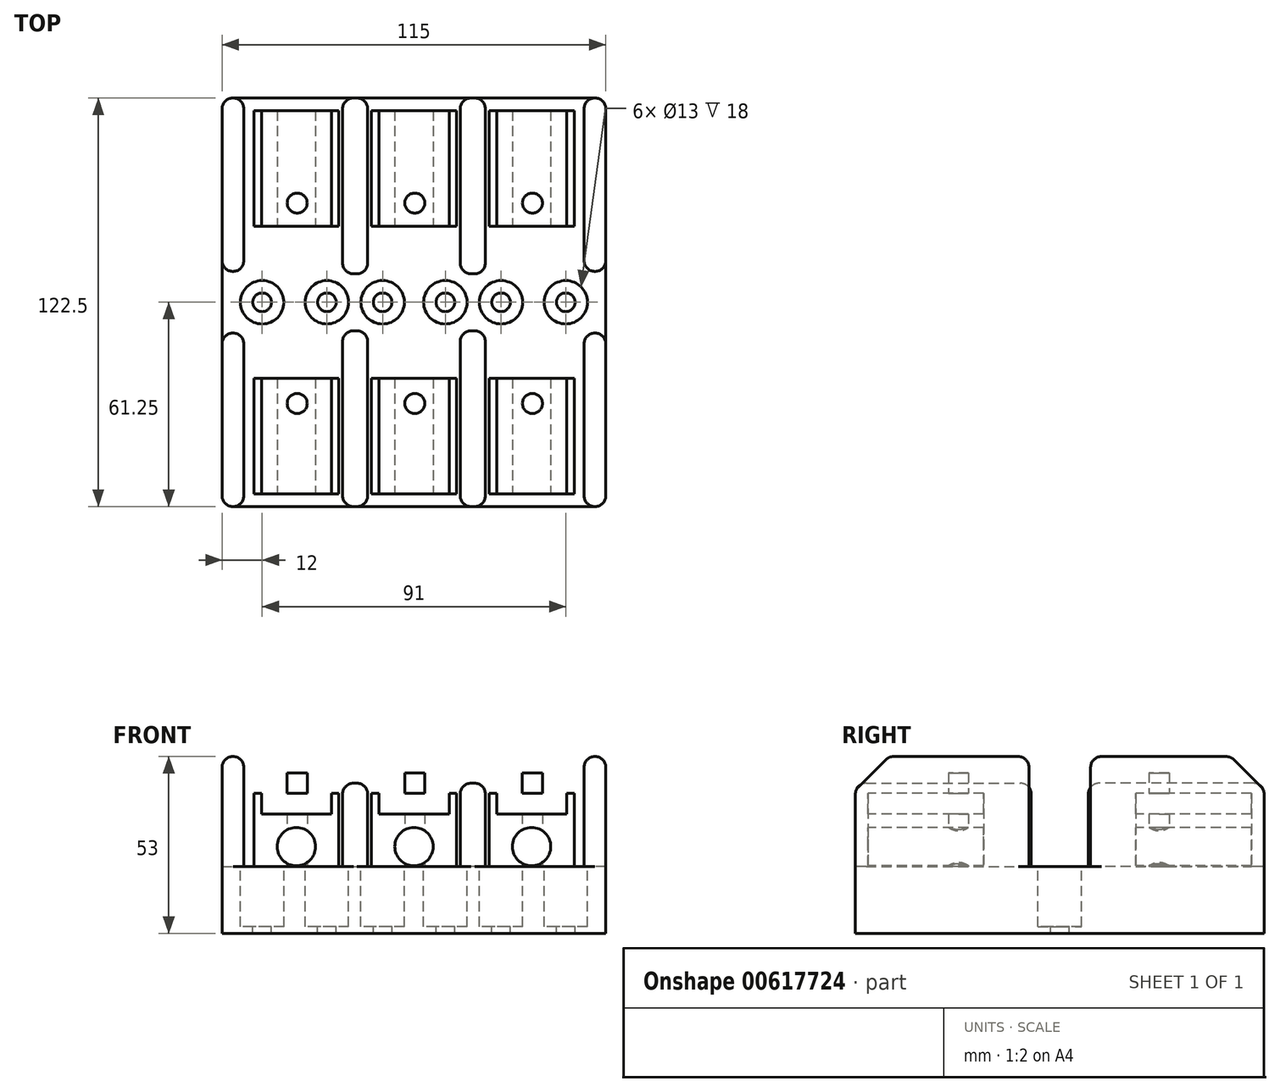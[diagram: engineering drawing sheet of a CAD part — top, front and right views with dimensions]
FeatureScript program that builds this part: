
annotation { "Feature Type Name" : "Feature", "Feature Type Description" : "" }
export const myFeature = defineFeature(function(context is Context, id is Id, definition is map)
    precondition{}
    {
        {
            var Q0;
            Q0=qCreatedBy(makeId("Top.planeOp"),FACE);
            var sketch = newSketch(context, id + "F0", { "sketchPlane" : qUnion([Q0])});
            skLineSegment(sketch, "E0.bottom", {"start": v(0, 0) * mm, "end": v(115, 0) * mm});
            skLineSegment(sketch, "E0.top", {"start": v(0, 122.5) * mm, "end": v(115, 122.5) * mm});
            skLineSegment(sketch, "E0.left", {"start": v(0, 0) * mm, "end": v(0, 122.5) * mm});
            skLineSegment(sketch, "E0.right", {"start": v(115, 0) * mm, "end": v(115, 122.5) * mm});
            skSolve(sketch);
        }
        {
            var Q0;
            Q0 = qSketchRegion(id + "F0", true);
            extrude(context, id + "F1", {"entities" : qUnion([Q0]), "depth" : 20 * mm, "offsetDistance" : 25 * mm});
        }
        {
            var Q0;
            Q0=makeQuery(id+"F1.opExtrude","CAP_FACE",FACE,{"disambiguationData":[OSD([sQuery(id+"F0.wireOp",EDGE,"E0.bottom"),sQuery(id+"F0.wireOp",EDGE,"E0.top"),sQuery(id+"F0.wireOp",EDGE,"E0.left"),sQuery(id+"F0.wireOp",EDGE,"E0.right")])],"isStart":false});
            var sketch = newSketch(context, id + "F2", { "sketchPlane" : qUnion([Q0])});
            skCircle(sketch, "E1", {"center": v(12, 61.25) * mm, "radius": 6.5 * mm});
            skPoint(sketch, "E1.centerSnap0", {"position": v(0, 61.25) * mm});
            skCircle(sketch, "E2", {"center": v(31.4, 61.25) * mm, "radius": 6.5 * mm});
            skCircle(sketch, "E3", {"center": v(48.1, 61.25) * mm, "radius": 6.5 * mm});
            skCircle(sketch, "E4.MirrorC", {"center": v(103, 61.25) * mm, "radius": 6.5 * mm});
            skCircle(sketch, "E5.MirrorC", {"center": v(83.6, 61.25) * mm, "radius": 6.5 * mm});
            skCircle(sketch, "E6.MirrorC", {"center": v(66.9, 61.25) * mm, "radius": 6.5 * mm});
            skSolve(sketch);
        }
        {
            var Q0;
            Q0 = qSketchRegion(id + "F2", true);
            extrude(context, id + "F3", {"entities" : qUnion([Q0]), "operationType" : NewBodyOperationType.REMOVE, "oppositeDirection" : true, "depth" : 18 * mm, "offsetDistance" : 25 * mm});
        }
        {
            var Q0;
            Q0=makeQuery(id+"F1.opExtrude","CAP_FACE",FACE,{"disambiguationData":[OSD([sQuery(id+"F0.wireOp",EDGE,"E0.bottom"),sQuery(id+"F0.wireOp",EDGE,"E0.top"),sQuery(id+"F0.wireOp",EDGE,"E0.left"),sQuery(id+"F0.wireOp",EDGE,"E0.right")])],"isStart":false});
            var sketch = newSketch(context, id + "F4", { "sketchPlane" : qUnion([Q0])});
            skCircle(sketch, "E7", {"center": v(12, 61.25) * mm, "radius": 2.8 * mm});
            skCircle(sketch, "E8", {"center": v(31.4, 61.25) * mm, "radius": 2.8 * mm});
            skCircle(sketch, "E9", {"center": v(48.1, 61.25) * mm, "radius": 2.8 * mm});
            skCircle(sketch, "E10", {"center": v(66.9, 61.25) * mm, "radius": 2.8 * mm});
            skCircle(sketch, "E11", {"center": v(83.6, 61.25) * mm, "radius": 2.8 * mm});
            skCircle(sketch, "E12", {"center": v(103, 61.25) * mm, "radius": 2.8 * mm});
            skSolve(sketch);
        }
        {
            var Q0;
            Q0 = qSketchRegion(id + "F4", true);
            extrude(context, id + "F5", {"entities" : qUnion([Q0]), "operationType" : NewBodyOperationType.REMOVE, "endBound" : BoundingType.THROUGH_ALL, "oppositeDirection" : true, "depth" : 25 * mm, "offsetDistance" : 25 * mm});
        }
        {
            var Q0;
            Q0=makeQuery(id+"F2.imprint","IMPRINT",FACE,{"disambiguationData":[TD([[makeQuery(id+"F2.imprint","IMPRINT",EDGE,{"derivedFrom":sQuery(id+"F2.wireOp",EDGE,"E1")}),-1.0]])]});
            var sketch = newSketch(context, id + "F6", { "sketchPlane" : qUnion([Q0])});
            skLineSegment(sketch, "E13.bottom", {"start": v(35, 84) * mm, "end": v(9.5, 84) * mm});
            skLineSegment(sketch, "E13.top", {"start": v(35, 118.7) * mm, "end": v(9.5, 118.7) * mm});
            skLineSegment(sketch, "E13.left", {"start": v(35, 84) * mm, "end": v(35, 118.7) * mm});
            skLineSegment(sketch, "E13.right", {"start": v(9.5, 84) * mm, "end": v(9.5, 118.7) * mm});
            skPoint(sketch, "E13.middle", {"position": v(22.25, 101.35) * mm});
            skLineSegment(sketch, "E14.bottom", {"start": v(70.25, 84) * mm, "end": v(44.75, 84) * mm});
            skLineSegment(sketch, "E14.top", {"start": v(70.25, 118.7) * mm, "end": v(44.75, 118.7) * mm});
            skLineSegment(sketch, "E14.left", {"start": v(70.25, 84) * mm, "end": v(70.25, 118.7) * mm});
            skLineSegment(sketch, "E14.right", {"start": v(44.75, 84) * mm, "end": v(44.75, 118.7) * mm});
            skPoint(sketch, "E14.middle", {"position": v(57.5, 101.35) * mm});
            skLineSegment(sketch, "E15.bottom", {"start": v(105.5, 84) * mm, "end": v(80, 84) * mm});
            skLineSegment(sketch, "E15.top", {"start": v(105.5, 118.7) * mm, "end": v(80, 118.7) * mm});
            skLineSegment(sketch, "E15.left", {"start": v(105.5, 84) * mm, "end": v(105.5, 118.7) * mm});
            skLineSegment(sketch, "E15.right", {"start": v(80, 84) * mm, "end": v(80, 118.7) * mm});
            skPoint(sketch, "E15.middle", {"position": v(92.75, 101.35) * mm});
            skLineSegment(sketch, "E16", {"start": v(0, 61.22) * mm, "end": v(114.99, 61.22) * mm});
            skLineSegment(sketch, "E17.MirrorCS", {"start": v(35, 3.73) * mm, "end": v(9.5, 3.73) * mm});
            skLineSegment(sketch, "E18.MirrorCS", {"start": v(35, 38.43) * mm, "end": v(9.5, 38.43) * mm});
            skPoint(sketch, "E19.MirrorP", {"position": v(57.5, 21.08) * mm});
            skLineSegment(sketch, "E20.MirrorCS", {"start": v(35, 38.43) * mm, "end": v(35, 3.73) * mm});
            skLineSegment(sketch, "E21.MirrorCS", {"start": v(9.5, 38.43) * mm, "end": v(9.5, 3.73) * mm});
            skLineSegment(sketch, "E22.MirrorCS", {"start": v(70.25, 38.43) * mm, "end": v(44.75, 38.43) * mm});
            skLineSegment(sketch, "E23.MirrorCS", {"start": v(70.25, 3.73) * mm, "end": v(44.75, 3.73) * mm});
            skLineSegment(sketch, "E24.MirrorCS", {"start": v(105.5, 38.43) * mm, "end": v(80, 38.43) * mm});
            skPoint(sketch, "E25.MirrorP", {"position": v(22.25, 21.08) * mm});
            skLineSegment(sketch, "E26.MirrorCS", {"start": v(70.25, 38.43) * mm, "end": v(70.25, 3.73) * mm});
            skPoint(sketch, "E27.MirrorP", {"position": v(92.75, 21.08) * mm});
            skLineSegment(sketch, "E28.MirrorCS", {"start": v(105.5, 38.43) * mm, "end": v(105.5, 3.73) * mm});
            skLineSegment(sketch, "E29.MirrorCS", {"start": v(80, 38.43) * mm, "end": v(80, 3.73) * mm});
            skLineSegment(sketch, "E30.MirrorCS", {"start": v(44.75, 38.43) * mm, "end": v(44.75, 3.73) * mm});
            skLineSegment(sketch, "E31.MirrorCS", {"start": v(105.5, 3.73) * mm, "end": v(80, 3.73) * mm});
            skSolve(sketch);
        }
        {
            var Q0;
            Q0 = qSketchRegion(id + "F6", true);
            extrude(context, id + "F7", {"entities" : qUnion([Q0]), "operationType" : NewBodyOperationType.ADD, "depth" : 22 * mm, "offsetDistance" : 25 * mm});
        }
        {
            var Q0;
            Q0=makeQuery(id+"F2.imprint","IMPRINT",FACE,{"disambiguationData":[TD([[makeQuery(id+"F2.imprint","IMPRINT",EDGE,{"derivedFrom":sQuery(id+"F2.wireOp",EDGE,"E1")}),-1.0]])]});
            var sketch = newSketch(context, id + "F8", { "sketchPlane" : qUnion([Q0])});
            skLineSegment(sketch, "E32.bottom", {"start": v(0, 0) * mm, "end": v(6.5, 0) * mm});
            skLineSegment(sketch, "E32.top", {"start": v(0, 52) * mm, "end": v(6.5, 52) * mm});
            skLineSegment(sketch, "E32.left", {"start": v(0, 0) * mm, "end": v(0, 52) * mm});
            skLineSegment(sketch, "E32.right", {"start": v(6.5, 0) * mm, "end": v(6.5, 52) * mm});
            skLineSegment(sketch, "E33.bottom", {"start": v(115, 122.5) * mm, "end": v(108.5, 122.5) * mm});
            skLineSegment(sketch, "E33.top", {"start": v(115, 70.5) * mm, "end": v(108.5, 70.5) * mm});
            skLineSegment(sketch, "E33.left", {"start": v(115, 122.5) * mm, "end": v(115, 70.5) * mm});
            skLineSegment(sketch, "E33.right", {"start": v(108.5, 122.5) * mm, "end": v(108.5, 70.5) * mm});
            skLineSegment(sketch, "E34.bottom", {"start": v(115, 0) * mm, "end": v(108.5, 0) * mm});
            skLineSegment(sketch, "E34.top", {"start": v(115, 52) * mm, "end": v(108.5, 52) * mm});
            skLineSegment(sketch, "E34.left", {"start": v(115, 0) * mm, "end": v(115, 52) * mm});
            skLineSegment(sketch, "E34.right", {"start": v(108.5, 0) * mm, "end": v(108.5, 52) * mm});
            skLineSegment(sketch, "E35.bottom", {"start": v(0, 70.5) * mm, "end": v(6.5, 70.5) * mm});
            skLineSegment(sketch, "E35.top", {"start": v(0, 122.5) * mm, "end": v(6.5, 122.5) * mm});
            skLineSegment(sketch, "E35.left", {"start": v(0, 70.5) * mm, "end": v(0, 122.5) * mm});
            skLineSegment(sketch, "E35.right", {"start": v(6.5, 70.5) * mm, "end": v(6.5, 122.5) * mm});
            skSolve(sketch);
        }
        {
            var Q0;
            Q0 = qSketchRegion(id + "F8", true);
            extrude(context, id + "F9", {"entities" : qUnion([Q0]), "operationType" : NewBodyOperationType.ADD, "depth" : 33 * mm, "offsetDistance" : 25 * mm});
        }
        {
            var Q0;
            Q0=makeQuery(id+"F2.imprint","IMPRINT",FACE,{"disambiguationData":[TD([[makeQuery(id+"F2.imprint","IMPRINT",EDGE,{"derivedFrom":sQuery(id+"F2.wireOp",EDGE,"E1")}),-1.0]])]});
            var sketch = newSketch(context, id + "F10", { "sketchPlane" : qUnion([Q0])});
            skLineSegment(sketch, "E36.bottom", {"start": v(36.13, 122.5) * mm, "end": v(43.63, 122.5) * mm});
            skLineSegment(sketch, "E36.top", {"start": v(36.13, 69.8) * mm, "end": v(43.63, 69.8) * mm});
            skLineSegment(sketch, "E36.left", {"start": v(36.13, 122.5) * mm, "end": v(36.13, 69.8) * mm});
            skLineSegment(sketch, "E36.right", {"start": v(43.63, 122.5) * mm, "end": v(43.63, 69.8) * mm});
            skLineSegment(sketch, "E37.bottom", {"start": v(36.13, 0) * mm, "end": v(43.63, 0) * mm});
            skLineSegment(sketch, "E37.top", {"start": v(36.13, 52.7) * mm, "end": v(43.63, 52.7) * mm});
            skLineSegment(sketch, "E37.left", {"start": v(36.13, 0) * mm, "end": v(36.13, 52.7) * mm});
            skLineSegment(sketch, "E37.right", {"start": v(43.63, 0) * mm, "end": v(43.63, 52.7) * mm});
            skLineSegment(sketch, "E38.bottom", {"start": v(71.38, 122.5) * mm, "end": v(78.88, 122.5) * mm});
            skLineSegment(sketch, "E38.top", {"start": v(71.38, 69.8) * mm, "end": v(78.88, 69.8) * mm});
            skLineSegment(sketch, "E38.left", {"start": v(71.38, 122.5) * mm, "end": v(71.38, 69.8) * mm});
            skLineSegment(sketch, "E38.right", {"start": v(78.88, 122.5) * mm, "end": v(78.88, 69.8) * mm});
            skLineSegment(sketch, "E39.bottom", {"start": v(78.88, 0) * mm, "end": v(71.38, 0) * mm});
            skLineSegment(sketch, "E39.top", {"start": v(78.88, 52.7) * mm, "end": v(71.38, 52.7) * mm});
            skLineSegment(sketch, "E39.left", {"start": v(78.88, 0) * mm, "end": v(78.88, 52.7) * mm});
            skLineSegment(sketch, "E39.right", {"start": v(71.38, 0) * mm, "end": v(71.38, 52.7) * mm});
            skSolve(sketch);
        }
        {
            var Q0;
            Q0 = qSketchRegion(id + "F10", true);
            extrude(context, id + "F11", {"entities" : qUnion([Q0]), "operationType" : NewBodyOperationType.ADD, "depth" : 25 * mm, "offsetDistance" : 25 * mm});
        }
        {
            var Q0;
            Q0=makeQuery(id+"F2.imprint","IMPRINT",FACE,{"disambiguationData":[TD([[makeQuery(id+"F2.imprint","IMPRINT",EDGE,{"derivedFrom":sQuery(id+"F2.wireOp",EDGE,"E1")}),-1.0]])]});
            var sketch = newSketch(context, id + "F12", { "sketchPlane" : qUnion([Q0])});
            skCircle(sketch, "E40", {"center": v(22.5, 91) * mm, "radius": 3 * mm});
            skCircle(sketch, "E41", {"center": v(57.75, 91) * mm, "radius": 3 * mm});
            skCircle(sketch, "E42", {"center": v(93, 91) * mm, "radius": 3 * mm});
            skCircle(sketch, "E43.MirrorC", {"center": v(22.5, 30.9) * mm, "radius": 3 * mm});
            skCircle(sketch, "E44.MirrorC", {"center": v(57.75, 30.9) * mm, "radius": 3 * mm});
            skCircle(sketch, "E45.MirrorC", {"center": v(93, 30.9) * mm, "radius": 3 * mm});
            skSolve(sketch);
        }
        {
            var Q0;
            Q0 = qSketchRegion(id + "F12", true);
            extrude(context, id + "F13", {"entities" : qUnion([Q0]), "depth" : 28.1 * mm, "offsetDistance" : 25 * mm});
        }
        {
            var Q0;
            Q0=makeQuery(id+"F11.boolean.opBoolean","MERGE",FACE,{"derivedFrom":[makeQuery(id+"F9.boolean.opBoolean","MERGE",FACE,{"derivedFrom":[makeQuery(id+"F1.opExtrude","SWEPT_FACE",FACE,{"disambiguationData":[OSD([sQuery(id+"F0.wireOp",EDGE,"E0.bottom")])]}),makeQuery(id+"F9.opExtrude","SWEPT_FACE",FACE,{"disambiguationData":[OSD([sQuery(id+"F8.wireOp",EDGE,"E32.bottom")])]}),makeQuery(id+"F9.opExtrude","SWEPT_FACE",FACE,{"disambiguationData":[OSD([sQuery(id+"F8.wireOp",EDGE,"E34.bottom")])]})]}),makeQuery(id+"F11.opExtrude","SWEPT_FACE",FACE,{"disambiguationData":[OSD([sQuery(id+"F10.wireOp",EDGE,"E37.bottom")])]}),makeQuery(id+"F11.opExtrude","SWEPT_FACE",FACE,{"disambiguationData":[OSD([sQuery(id+"F10.wireOp",EDGE,"E39.bottom")])]})]});
            var sketch = newSketch(context, id + "F14", { "sketchPlane" : qUnion([Q0])});
            skCircle(sketch, "E46", {"center": v(22.25, 26) * mm, "radius": 5.75 * mm});
            skCircle(sketch, "E47", {"center": v(57.5, 26) * mm, "radius": 5.75 * mm});
            skCircle(sketch, "E48", {"center": v(92.75, 26) * mm, "radius": 5.75 * mm});
            skSolve(sketch);
        }
        {
            var Q0;
            Q0 = qSketchRegion(id + "F14", true);
            extrude(context, id + "F15", {"entities" : qUnion([Q0]), "operationType" : NewBodyOperationType.REMOVE, "endBound" : BoundingType.THROUGH_ALL, "oppositeDirection" : true, "depth" : 25 * mm, "offsetDistance" : 25 * mm});
        }
        {
            var Q0;
            Q0=makeQuery(id+"F7.opExtrude","CAP_FACE",FACE,{"disambiguationData":[OSD([sQuery(id+"F6.wireOp",EDGE,"E17.MirrorCS"),sQuery(id+"F6.wireOp",EDGE,"E18.MirrorCS"),sQuery(id+"F6.wireOp",EDGE,"E20.MirrorCS"),sQuery(id+"F6.wireOp",EDGE,"E21.MirrorCS")])],"isStart":false});
            var sketch = newSketch(context, id + "F16", { "sketchPlane" : qUnion([Q0])});
            skLineSegment(sketch, "E49.bottom", {"start": v(11.8, 38.43) * mm, "end": v(32.8, 38.43) * mm});
            skLineSegment(sketch, "E49.top", {"start": v(11.8, 3.73) * mm, "end": v(32.8, 3.73) * mm});
            skLineSegment(sketch, "E49.left", {"start": v(11.8, 38.43) * mm, "end": v(11.8, 3.73) * mm});
            skLineSegment(sketch, "E49.right", {"start": v(32.8, 38.43) * mm, "end": v(32.8, 3.73) * mm});
            skSolve(sketch);
        }
        {
            var Q0;
            Q0 = qSketchRegion(id + "F16", true);
            extrude(context, id + "F17", {"entities" : qUnion([Q0]), "operationType" : NewBodyOperationType.REMOVE, "oppositeDirection" : true, "depth" : 6.2 * mm, "offsetDistance" : 25 * mm});
        }
        {
            var Q0;
            Q0=makeQuery(id+"F7.opExtrude","CAP_FACE",FACE,{"disambiguationData":[OSD([sQuery(id+"F6.wireOp",EDGE,"E22.MirrorCS"),sQuery(id+"F6.wireOp",EDGE,"E23.MirrorCS"),sQuery(id+"F6.wireOp",EDGE,"E26.MirrorCS"),sQuery(id+"F6.wireOp",EDGE,"E30.MirrorCS")])],"isStart":false});
            var sketch = newSketch(context, id + "F18", { "sketchPlane" : qUnion([Q0])});
            skLineSegment(sketch, "E50.bottom", {"start": v(47.05, 38.43) * mm, "end": v(68.05, 38.43) * mm});
            skLineSegment(sketch, "E50.top", {"start": v(47.05, 3.73) * mm, "end": v(68.05, 3.73) * mm});
            skLineSegment(sketch, "E50.left", {"start": v(47.05, 38.43) * mm, "end": v(47.05, 3.73) * mm});
            skLineSegment(sketch, "E50.right", {"start": v(68.05, 38.43) * mm, "end": v(68.05, 3.73) * mm});
            skSolve(sketch);
        }
        {
            var Q0;
            Q0 = qSketchRegion(id + "F18", true);
            extrude(context, id + "F19", {"entities" : qUnion([Q0]), "operationType" : NewBodyOperationType.REMOVE, "oppositeDirection" : true, "depth" : 6.2 * mm, "offsetDistance" : 25 * mm});
        }
        {
            var Q0;
            Q0=makeQuery(id+"F7.opExtrude","CAP_FACE",FACE,{"disambiguationData":[OSD([sQuery(id+"F6.wireOp",EDGE,"E24.MirrorCS"),sQuery(id+"F6.wireOp",EDGE,"E28.MirrorCS"),sQuery(id+"F6.wireOp",EDGE,"E29.MirrorCS"),sQuery(id+"F6.wireOp",EDGE,"E31.MirrorCS")])],"isStart":false});
            var sketch = newSketch(context, id + "F20", { "sketchPlane" : qUnion([Q0])});
            skLineSegment(sketch, "E51.bottom", {"start": v(82.3, 38.43) * mm, "end": v(103.3, 38.43) * mm});
            skLineSegment(sketch, "E51.top", {"start": v(82.3, 3.73) * mm, "end": v(103.3, 3.73) * mm});
            skLineSegment(sketch, "E51.left", {"start": v(82.3, 38.43) * mm, "end": v(82.3, 3.73) * mm});
            skLineSegment(sketch, "E51.right", {"start": v(103.3, 38.43) * mm, "end": v(103.3, 3.73) * mm});
            skSolve(sketch);
        }
        {
            var Q0;
            Q0 = qSketchRegion(id + "F20", true);
            extrude(context, id + "F21", {"entities" : qUnion([Q0]), "operationType" : NewBodyOperationType.REMOVE, "oppositeDirection" : true, "depth" : 6.2 * mm, "offsetDistance" : 25 * mm});
        }
        {
            var Q0;
            Q0=makeQuery(id+"F7.opExtrude","CAP_FACE",FACE,{"disambiguationData":[OSD([sQuery(id+"F6.wireOp",EDGE,"E13.bottom"),sQuery(id+"F6.wireOp",EDGE,"E13.top"),sQuery(id+"F6.wireOp",EDGE,"E13.left"),sQuery(id+"F6.wireOp",EDGE,"E13.right")])],"isStart":false});
            var sketch = newSketch(context, id + "F22", { "sketchPlane" : qUnion([Q0])});
            skLineSegment(sketch, "E52.bottom", {"start": v(11.8, 118.7) * mm, "end": v(32.8, 118.7) * mm});
            skLineSegment(sketch, "E52.top", {"start": v(11.8, 84) * mm, "end": v(32.8, 84) * mm});
            skLineSegment(sketch, "E52.left", {"start": v(11.8, 118.7) * mm, "end": v(11.8, 84) * mm});
            skLineSegment(sketch, "E52.right", {"start": v(32.8, 118.7) * mm, "end": v(32.8, 84) * mm});
            skSolve(sketch);
        }
        {
            var Q0;
            Q0 = qSketchRegion(id + "F22", true);
            extrude(context, id + "F23", {"entities" : qUnion([Q0]), "operationType" : NewBodyOperationType.REMOVE, "oppositeDirection" : true, "depth" : 6.2 * mm, "offsetDistance" : 25 * mm});
        }
        {
            var Q0;
            Q0=makeQuery(id+"F7.opExtrude","CAP_FACE",FACE,{"disambiguationData":[OSD([sQuery(id+"F6.wireOp",EDGE,"E14.bottom"),sQuery(id+"F6.wireOp",EDGE,"E14.top"),sQuery(id+"F6.wireOp",EDGE,"E14.left"),sQuery(id+"F6.wireOp",EDGE,"E14.right")])],"isStart":false});
            var sketch = newSketch(context, id + "F24", { "sketchPlane" : qUnion([Q0])});
            skLineSegment(sketch, "E53.bottom", {"start": v(47.05, 118.7) * mm, "end": v(68.05, 118.7) * mm});
            skLineSegment(sketch, "E53.top", {"start": v(47.05, 84) * mm, "end": v(68.05, 84) * mm});
            skLineSegment(sketch, "E53.left", {"start": v(47.05, 118.7) * mm, "end": v(47.05, 84) * mm});
            skLineSegment(sketch, "E53.right", {"start": v(68.05, 118.7) * mm, "end": v(68.05, 84) * mm});
            skSolve(sketch);
        }
        {
            var Q0;
            Q0 = qSketchRegion(id + "F24", true);
            extrude(context, id + "F25", {"entities" : qUnion([Q0]), "operationType" : NewBodyOperationType.REMOVE, "oppositeDirection" : true, "depth" : 6.2 * mm, "offsetDistance" : 25 * mm});
        }
        {
            var Q0;
            Q0=makeQuery(id+"F7.opExtrude","CAP_FACE",FACE,{"disambiguationData":[OSD([sQuery(id+"F6.wireOp",EDGE,"E15.bottom"),sQuery(id+"F6.wireOp",EDGE,"E15.top"),sQuery(id+"F6.wireOp",EDGE,"E15.left"),sQuery(id+"F6.wireOp",EDGE,"E15.right")])],"isStart":false});
            var sketch = newSketch(context, id + "F26", { "sketchPlane" : qUnion([Q0])});
            skLineSegment(sketch, "E54.bottom", {"start": v(82.3, 118.7) * mm, "end": v(103.3, 118.7) * mm});
            skLineSegment(sketch, "E54.top", {"start": v(82.3, 84) * mm, "end": v(103.3, 84) * mm});
            skLineSegment(sketch, "E54.left", {"start": v(82.3, 118.7) * mm, "end": v(82.3, 84) * mm});
            skLineSegment(sketch, "E54.right", {"start": v(103.3, 118.7) * mm, "end": v(103.3, 84) * mm});
            skSolve(sketch);
        }
        {
            var Q0;
            Q0 = qSketchRegion(id + "F26", true);
            extrude(context, id + "F27", {"entities" : qUnion([Q0]), "operationType" : NewBodyOperationType.REMOVE, "oppositeDirection" : true, "depth" : 6.2 * mm, "offsetDistance" : 25 * mm});
        }
        {
            var Q0;
            Q0=makeQuery(id+"F9.opExtrude","CAP_EDGE",EDGE,{"disambiguationData":[OSD([sQuery(id+"F8.wireOp",EDGE,"E32.bottom")])],"isStart":false});
            var Q1;
            Q1=makeQuery(id+"F9.opExtrude","CAP_EDGE",EDGE,{"disambiguationData":[OSD([sQuery(id+"F8.wireOp",EDGE,"E34.bottom")])],"isStart":false});
            var Q2;
            Q2=makeQuery(id+"F9.opExtrude","CAP_EDGE",EDGE,{"disambiguationData":[OSD([sQuery(id+"F8.wireOp",EDGE,"E33.bottom")])],"isStart":false});
            var Q3;
            Q3=makeQuery(id+"F9.opExtrude","CAP_EDGE",EDGE,{"disambiguationData":[OSD([sQuery(id+"F8.wireOp",EDGE,"E35.top")])],"isStart":false});
            chamfer(context, id + "F28", {"entities" : qUnion([Q0, Q1, Q2, Q3]), "width" : 10 * mm, "tangentPropagation" : true});
        }
        {
            var Q0;
            Q0=makeQuery(id+"F9.opExtrude","CAP_EDGE",EDGE,{"disambiguationData":[OSD([sQuery(id+"F8.wireOp",EDGE,"E35.right")])],"isStart":false});
            var Q1;
            Q1=makeQuery(id+"F9.opExtrude","CAP_EDGE",EDGE,{"disambiguationData":[OSD([sQuery(id+"F8.wireOp",EDGE,"E35.bottom")])],"isStart":false});
            var Q2;
            Q2=makeQuery(id+"F9.opExtrude","CAP_EDGE",EDGE,{"disambiguationData":[OSD([sQuery(id+"F8.wireOp",EDGE,"E35.left")])],"isStart":false});
            var Q3;
            Q3=makeQuery(id+"F11.opExtrude","CAP_FACE",FACE,{"disambiguationData":[OSD([sQuery(id+"F10.wireOp",EDGE,"E36.bottom"),sQuery(id+"F10.wireOp",EDGE,"E36.top"),sQuery(id+"F10.wireOp",EDGE,"E36.left"),sQuery(id+"F10.wireOp",EDGE,"E36.right")])],"isStart":false});
            var Q4;
            Q4=makeQuery(id+"F11.opExtrude","CAP_FACE",FACE,{"disambiguationData":[OSD([sQuery(id+"F10.wireOp",EDGE,"E38.bottom"),sQuery(id+"F10.wireOp",EDGE,"E38.top"),sQuery(id+"F10.wireOp",EDGE,"E38.left"),sQuery(id+"F10.wireOp",EDGE,"E38.right")])],"isStart":false});
            var Q5;
            Q5=makeQuery(id+"F11.opExtrude","CAP_FACE",FACE,{"disambiguationData":[OSD([sQuery(id+"F10.wireOp",EDGE,"E39.bottom"),sQuery(id+"F10.wireOp",EDGE,"E39.top"),sQuery(id+"F10.wireOp",EDGE,"E39.left"),sQuery(id+"F10.wireOp",EDGE,"E39.right")])],"isStart":false});
            var Q6;
            Q6=makeQuery(id+"F11.opExtrude","CAP_FACE",FACE,{"disambiguationData":[OSD([sQuery(id+"F10.wireOp",EDGE,"E37.bottom"),sQuery(id+"F10.wireOp",EDGE,"E37.top"),sQuery(id+"F10.wireOp",EDGE,"E37.left"),sQuery(id+"F10.wireOp",EDGE,"E37.right")])],"isStart":false});
            var Q7;
            Q7=makeQuery(id+"F9.opExtrude","CAP_FACE",FACE,{"disambiguationData":[OSD([sQuery(id+"F8.wireOp",EDGE,"E32.bottom"),sQuery(id+"F8.wireOp",EDGE,"E32.top"),sQuery(id+"F8.wireOp",EDGE,"E32.left"),sQuery(id+"F8.wireOp",EDGE,"E32.right")])],"isStart":false});
            var Q8;
            Q8=makeQuery(id+"F28.opChamfer","BLEND_FACE",FACE,{"disambiguationData":[OSD([sQuery(id+"F8.wireOp",EDGE,"E32.bottom")])]});
            var Q9;
            Q9=makeQuery(id+"F28.opChamfer","BLEND_FACE",FACE,{"disambiguationData":[OSD([sQuery(id+"F8.wireOp",EDGE,"E34.bottom")])]});
            var Q10;
            Q10=makeQuery(id+"F9.opExtrude","CAP_FACE",FACE,{"disambiguationData":[OSD([sQuery(id+"F8.wireOp",EDGE,"E34.bottom"),sQuery(id+"F8.wireOp",EDGE,"E34.top"),sQuery(id+"F8.wireOp",EDGE,"E34.left"),sQuery(id+"F8.wireOp",EDGE,"E34.right")])],"isStart":false});
            var Q11;
            Q11=makeQuery(id+"F9.opExtrude","CAP_FACE",FACE,{"disambiguationData":[OSD([sQuery(id+"F8.wireOp",EDGE,"E33.bottom"),sQuery(id+"F8.wireOp",EDGE,"E33.top"),sQuery(id+"F8.wireOp",EDGE,"E33.left"),sQuery(id+"F8.wireOp",EDGE,"E33.right")])],"isStart":false});
            var Q12;
            Q12=makeQuery(id+"F11.opExtrude","SWEPT_EDGE",EDGE,{"disambiguationData":[OSD([sQuery(id+"F0.wireOp",EDGE,"E0.bottom"),sQuery(id+"F10.wireOp",EDGE,"E39.bottom"),sQuery(id+"F10.wireOp",EDGE,"E39.left")])]});
            var Q13;
            Q13=makeQuery(id+"F11.opExtrude","SWEPT_EDGE",EDGE,{"disambiguationData":[OSD([sQuery(id+"F0.wireOp",EDGE,"E0.bottom"),sQuery(id+"F10.wireOp",EDGE,"E39.bottom"),sQuery(id+"F10.wireOp",EDGE,"E39.right")])]});
            var Q14;
            Q14=makeQuery(id+"F11.opExtrude","SWEPT_EDGE",EDGE,{"disambiguationData":[OSD([sQuery(id+"F0.wireOp",EDGE,"E0.bottom"),sQuery(id+"F10.wireOp",EDGE,"E37.bottom"),sQuery(id+"F10.wireOp",EDGE,"E37.right")])]});
            var Q15;
            Q15=makeQuery(id+"F11.opExtrude","SWEPT_EDGE",EDGE,{"disambiguationData":[OSD([sQuery(id+"F0.wireOp",EDGE,"E0.bottom"),sQuery(id+"F10.wireOp",EDGE,"E37.bottom"),sQuery(id+"F10.wireOp",EDGE,"E37.left")])]});
            var Q16;
            Q16=makeQuery(id+"F9.opExtrude","SWEPT_EDGE",EDGE,{"disambiguationData":[OSD([sQuery(id+"F0.wireOp",EDGE,"E0.bottom"),sQuery(id+"F8.wireOp",EDGE,"E32.bottom"),sQuery(id+"F8.wireOp",EDGE,"E32.right")])]});
            var Q17;
            Q17=makeQuery(id+"F9.boolean.opBoolean","MERGE",EDGE,{"derivedFrom":[makeQuery(id+"F1.opExtrude","SWEPT_EDGE",EDGE,{"disambiguationData":[OSD([sQuery(id+"F0.wireOp",EDGE,"E0.bottom"),sQuery(id+"F0.wireOp",EDGE,"E0.left")])]}),makeQuery(id+"F9.opExtrude","SWEPT_EDGE",EDGE,{"disambiguationData":[OSD([sQuery(id+"F8.wireOp",EDGE,"E32.bottom"),sQuery(id+"F8.wireOp",EDGE,"E32.left")])]})]});
            var Q18;
            Q18=makeQuery(id+"F9.opExtrude","SWEPT_EDGE",EDGE,{"disambiguationData":[OSD([sQuery(id+"F0.wireOp",EDGE,"E0.bottom"),sQuery(id+"F8.wireOp",EDGE,"E34.bottom"),sQuery(id+"F8.wireOp",EDGE,"E34.right")])]});
            var Q19;
            Q19=makeQuery(id+"F9.boolean.opBoolean","MERGE",EDGE,{"derivedFrom":[makeQuery(id+"F1.opExtrude","SWEPT_EDGE",EDGE,{"disambiguationData":[OSD([sQuery(id+"F0.wireOp",EDGE,"E0.bottom"),sQuery(id+"F0.wireOp",EDGE,"E0.right")])]}),makeQuery(id+"F9.opExtrude","SWEPT_EDGE",EDGE,{"disambiguationData":[OSD([sQuery(id+"F8.wireOp",EDGE,"E34.bottom"),sQuery(id+"F8.wireOp",EDGE,"E34.left")])]})]});
            var Q20;
            Q20=makeQuery(id+"F9.opExtrude","SWEPT_EDGE",EDGE,{"disambiguationData":[OSD([sQuery(id+"F0.wireOp",EDGE,"E0.right"),sQuery(id+"F8.wireOp",EDGE,"E34.top"),sQuery(id+"F8.wireOp",EDGE,"E34.left")])]});
            var Q21;
            Q21=makeQuery(id+"F9.opExtrude","SWEPT_EDGE",EDGE,{"disambiguationData":[OSD([sQuery(id+"F8.wireOp",EDGE,"E34.top"),sQuery(id+"F8.wireOp",EDGE,"E34.right")])]});
            var Q22;
            Q22=makeQuery(id+"F11.opExtrude","SWEPT_EDGE",EDGE,{"disambiguationData":[OSD([sQuery(id+"F10.wireOp",EDGE,"E39.top"),sQuery(id+"F10.wireOp",EDGE,"E39.left")])]});
            var Q23;
            Q23=makeQuery(id+"F11.opExtrude","SWEPT_EDGE",EDGE,{"disambiguationData":[OSD([sQuery(id+"F10.wireOp",EDGE,"E39.top"),sQuery(id+"F10.wireOp",EDGE,"E39.right")])]});
            var Q24;
            Q24=makeQuery(id+"F11.opExtrude","SWEPT_EDGE",EDGE,{"disambiguationData":[OSD([sQuery(id+"F10.wireOp",EDGE,"E37.top"),sQuery(id+"F10.wireOp",EDGE,"E37.right")])]});
            var Q25;
            Q25=makeQuery(id+"F11.opExtrude","SWEPT_EDGE",EDGE,{"disambiguationData":[OSD([sQuery(id+"F10.wireOp",EDGE,"E37.top"),sQuery(id+"F10.wireOp",EDGE,"E37.left")])]});
            var Q26;
            Q26=makeQuery(id+"F9.opExtrude","SWEPT_EDGE",EDGE,{"disambiguationData":[OSD([sQuery(id+"F8.wireOp",EDGE,"E32.top"),sQuery(id+"F8.wireOp",EDGE,"E32.right")])]});
            var Q27;
            Q27=makeQuery(id+"F9.opExtrude","SWEPT_EDGE",EDGE,{"disambiguationData":[OSD([sQuery(id+"F0.wireOp",EDGE,"E0.left"),sQuery(id+"F8.wireOp",EDGE,"E32.top"),sQuery(id+"F8.wireOp",EDGE,"E32.left")])]});
            var Q28;
            Q28=makeQuery(id+"F9.boolean.opBoolean","MERGE",EDGE,{"derivedFrom":[makeQuery(id+"F1.opExtrude","SWEPT_EDGE",EDGE,{"disambiguationData":[OSD([sQuery(id+"F0.wireOp",EDGE,"E0.top"),sQuery(id+"F0.wireOp",EDGE,"E0.right")])]}),makeQuery(id+"F9.opExtrude","SWEPT_EDGE",EDGE,{"disambiguationData":[OSD([sQuery(id+"F8.wireOp",EDGE,"E33.bottom"),sQuery(id+"F8.wireOp",EDGE,"E33.left")])]})]});
            var Q29;
            Q29=makeQuery(id+"F28.opChamfer","BLEND_FACE",FACE,{"disambiguationData":[OSD([sQuery(id+"F8.wireOp",EDGE,"E33.bottom")])]});
            var Q30;
            Q30=makeQuery(id+"F9.opExtrude","SWEPT_EDGE",EDGE,{"disambiguationData":[OSD([sQuery(id+"F0.wireOp",EDGE,"E0.top"),sQuery(id+"F8.wireOp",EDGE,"E33.bottom"),sQuery(id+"F8.wireOp",EDGE,"E33.right")])]});
            var Q31;
            Q31=makeQuery(id+"F11.opExtrude","SWEPT_EDGE",EDGE,{"disambiguationData":[OSD([sQuery(id+"F0.wireOp",EDGE,"E0.top"),sQuery(id+"F10.wireOp",EDGE,"E38.bottom"),sQuery(id+"F10.wireOp",EDGE,"E38.right")])]});
            var Q32;
            Q32=makeQuery(id+"F11.opExtrude","SWEPT_EDGE",EDGE,{"disambiguationData":[OSD([sQuery(id+"F0.wireOp",EDGE,"E0.top"),sQuery(id+"F10.wireOp",EDGE,"E38.bottom"),sQuery(id+"F10.wireOp",EDGE,"E38.left")])]});
            var Q33;
            Q33=makeQuery(id+"F11.opExtrude","SWEPT_EDGE",EDGE,{"disambiguationData":[OSD([sQuery(id+"F0.wireOp",EDGE,"E0.top"),sQuery(id+"F10.wireOp",EDGE,"E36.bottom"),sQuery(id+"F10.wireOp",EDGE,"E36.right")])]});
            var Q34;
            Q34=makeQuery(id+"F11.opExtrude","SWEPT_EDGE",EDGE,{"disambiguationData":[OSD([sQuery(id+"F0.wireOp",EDGE,"E0.top"),sQuery(id+"F10.wireOp",EDGE,"E36.bottom"),sQuery(id+"F10.wireOp",EDGE,"E36.left")])]});
            var Q35;
            Q35=makeQuery(id+"F28.opChamfer","BLEND_FACE",FACE,{"disambiguationData":[OSD([sQuery(id+"F8.wireOp",EDGE,"E35.top")])]});
            var Q36;
            Q36=makeQuery(id+"F9.boolean.opBoolean","MERGE",EDGE,{"derivedFrom":[makeQuery(id+"F1.opExtrude","SWEPT_EDGE",EDGE,{"disambiguationData":[OSD([sQuery(id+"F0.wireOp",EDGE,"E0.top"),sQuery(id+"F0.wireOp",EDGE,"E0.left")])]}),makeQuery(id+"F9.opExtrude","SWEPT_EDGE",EDGE,{"disambiguationData":[OSD([sQuery(id+"F8.wireOp",EDGE,"E35.top"),sQuery(id+"F8.wireOp",EDGE,"E35.left")])]})]});
            var Q37;
            Q37=makeQuery(id+"F9.opExtrude","SWEPT_EDGE",EDGE,{"disambiguationData":[OSD([sQuery(id+"F0.wireOp",EDGE,"E0.top"),sQuery(id+"F8.wireOp",EDGE,"E35.top"),sQuery(id+"F8.wireOp",EDGE,"E35.right")])]});
            var Q38;
            Q38=makeQuery(id+"F9.opExtrude","SWEPT_EDGE",EDGE,{"disambiguationData":[OSD([sQuery(id+"F0.wireOp",EDGE,"E0.right"),sQuery(id+"F8.wireOp",EDGE,"E33.top"),sQuery(id+"F8.wireOp",EDGE,"E33.left")])]});
            var Q39;
            Q39=makeQuery(id+"F9.opExtrude","SWEPT_EDGE",EDGE,{"disambiguationData":[OSD([sQuery(id+"F8.wireOp",EDGE,"E33.top"),sQuery(id+"F8.wireOp",EDGE,"E33.right")])]});
            var Q40;
            Q40=makeQuery(id+"F11.opExtrude","SWEPT_EDGE",EDGE,{"disambiguationData":[OSD([sQuery(id+"F10.wireOp",EDGE,"E38.top"),sQuery(id+"F10.wireOp",EDGE,"E38.right")])]});
            var Q41;
            Q41=makeQuery(id+"F11.opExtrude","SWEPT_EDGE",EDGE,{"disambiguationData":[OSD([sQuery(id+"F10.wireOp",EDGE,"E38.top"),sQuery(id+"F10.wireOp",EDGE,"E38.left")])]});
            var Q42;
            Q42=makeQuery(id+"F11.opExtrude","SWEPT_EDGE",EDGE,{"disambiguationData":[OSD([sQuery(id+"F10.wireOp",EDGE,"E36.top"),sQuery(id+"F10.wireOp",EDGE,"E36.right")])]});
            var Q43;
            Q43=makeQuery(id+"F11.opExtrude","SWEPT_EDGE",EDGE,{"disambiguationData":[OSD([sQuery(id+"F10.wireOp",EDGE,"E36.top"),sQuery(id+"F10.wireOp",EDGE,"E36.left")])]});
            var Q44;
            Q44=makeQuery(id+"F9.opExtrude","SWEPT_EDGE",EDGE,{"disambiguationData":[OSD([sQuery(id+"F8.wireOp",EDGE,"E35.bottom"),sQuery(id+"F8.wireOp",EDGE,"E35.right")])]});
            var Q45;
            Q45=makeQuery(id+"F9.opExtrude","SWEPT_EDGE",EDGE,{"disambiguationData":[OSD([sQuery(id+"F0.wireOp",EDGE,"E0.left"),sQuery(id+"F8.wireOp",EDGE,"E35.bottom"),sQuery(id+"F8.wireOp",EDGE,"E35.left")])]});
            fillet(context, id + "F29", {"entities" : qUnion([Q0, Q1, Q2, Q3, Q4, Q5, Q6, Q7, Q8, Q9, Q10, Q11, Q12, Q13, Q14, Q15, Q16, Q17, Q18, Q19, Q20, Q21, Q22, Q23, Q24, Q25, Q26, Q27, Q28, Q29, Q30, Q31, Q32, Q33, Q34, Q35, Q36, Q37, Q38, Q39, Q40, Q41, Q42, Q43, Q44, Q45]), "radius" : 3.2 * mm, "tangentPropagation" : true, "allowEdgeOverflow" : false});
        }
    });
